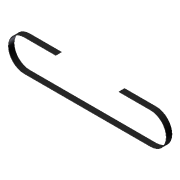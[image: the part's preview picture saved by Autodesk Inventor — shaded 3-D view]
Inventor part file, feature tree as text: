
AUTODESK INVENTOR PART (.ipt)
format: ipt  version: unknown  size: 196,608 bytes
history: native  units: in
note: dims shown in document units (in); Inventor stores cm internally (conversion verified against a paired STEP export)
features: sketch x4, extrude x2, sweep x1
ambient origin geometry x8: Origin, YZ Plane, XZ Plane, XY Plane, X Axis, Y Axis, Z Axis, Center Point
feature tree (7):
  sweep  "Sweep6"
  extrude  "Extrusion5"  Depth=0.3543in
  extrude  "Extrusion6"  Depth=0.0394in
  sketch  "Sketch9"  dims[d49=3.937in d50=15.748in]
  sketch  "Sketch14"  dims[d51=0.7087in d52=0.3543in]
  sketch  "Sketch16"  dims[d53=0.0197in d54=0.0394in]
  sketch  "Sketch17"  dims[d58=0.9843in d59=1.9685in d60=1.9685in d61=1.9685in d62=1.9685in d63=0.0in d64=3.937in d65=0.0in d66=3.937in d67=0.0in]
